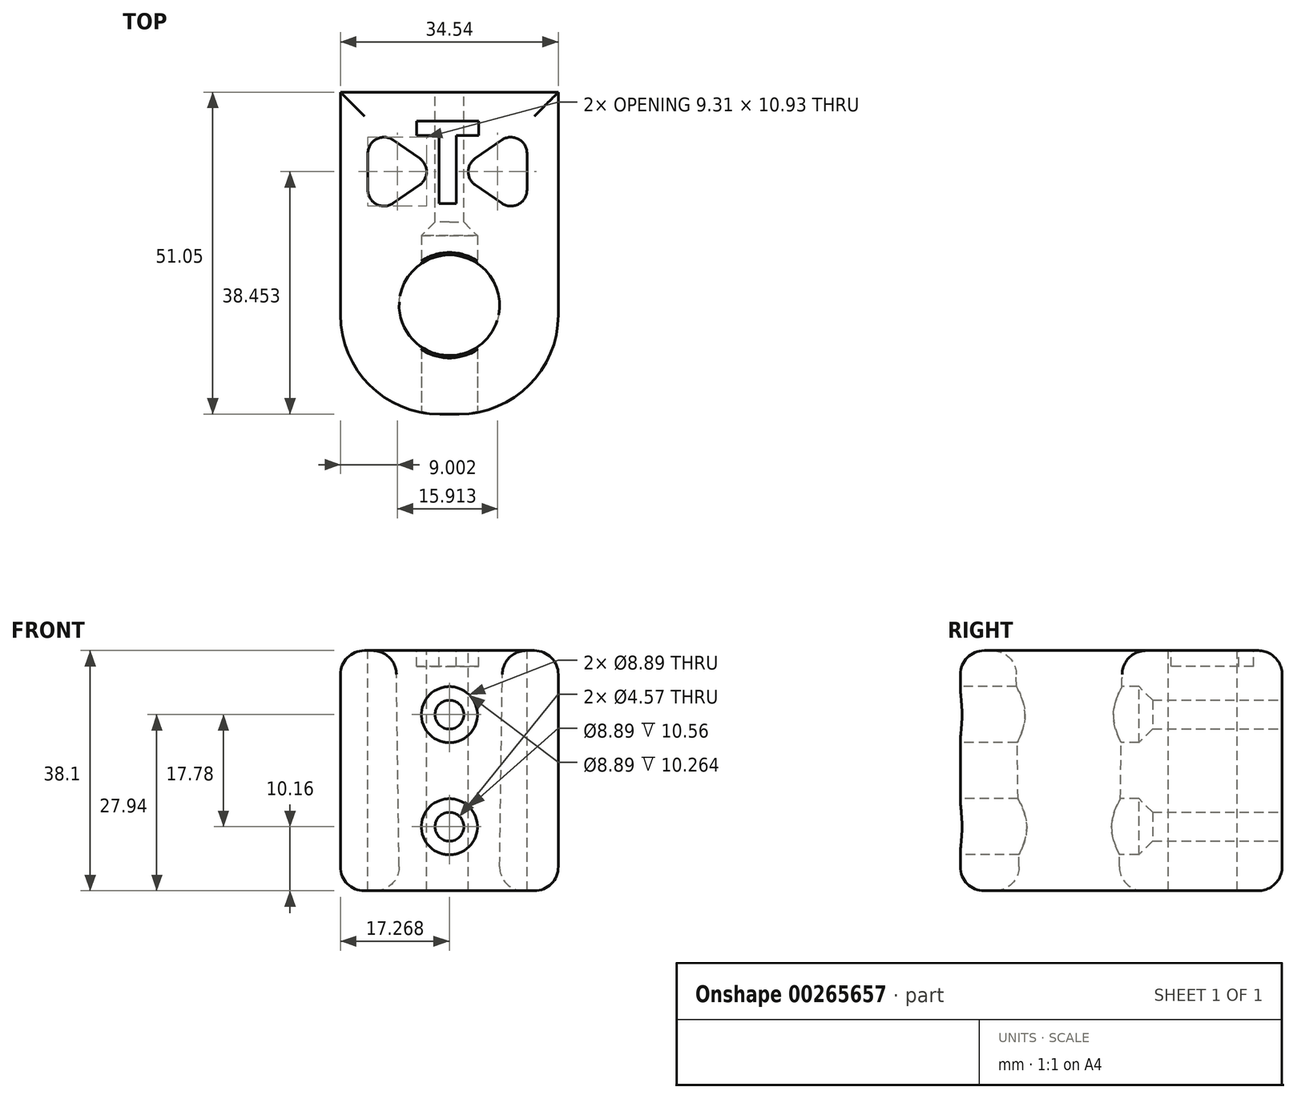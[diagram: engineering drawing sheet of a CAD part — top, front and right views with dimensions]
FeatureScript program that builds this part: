
annotation { "Feature Type Name" : "Feature", "Feature Type Description" : "" }
export const myFeature = defineFeature(function(context is Context, id is Id, definition is map)
    precondition{}
    {
        {
            var Q0;
            Q0=qCreatedBy(makeId("Top.planeOp"),FACE);
            var sketch = newSketch(context, id + "F0", { "sketchPlane" : qUnion([Q0])});
            skLineSegment(sketch, "E0.bottom", {"start": v(0, 0) * mm, "end": v(34.54, 0) * mm});
            skLineSegment(sketch, "E0.top", {"start": v(0, -34.54) * mm, "end": v(34.54, -34.54) * mm});
            skLineSegment(sketch, "E0.left", {"start": v(0, 0) * mm, "end": v(0, -34.54) * mm});
            skLineSegment(sketch, "E0.right", {"start": v(34.54, 0) * mm, "end": v(34.54, -34.54) * mm});
            skSolve(sketch);
        }
        {
            var Q0;
            Q0 = qSketchRegion(id + "F0", true);
            extrude(context, id + "F1", {"entities" : qUnion([Q0]), "depth" : 38.1 * mm});
        }
        {
            var Q0;
            Q0=makeQuery(id+"F1.opExtrude","CAP_FACE",FACE,{"disambiguationData":[OSD([sQuery(id+"F0.wireOp",EDGE,"E0.bottom"),sQuery(id+"F0.wireOp",EDGE,"E0.top"),sQuery(id+"F0.wireOp",EDGE,"E0.left"),sQuery(id+"F0.wireOp",EDGE,"E0.right")])],"isStart":false});
            var sketch = newSketch(context, id + "F2", { "sketchPlane" : qUnion([Q0])});
            skCircle(sketch, "E1", {"center": v(17.27, -17.27) * mm, "radius": 8.45 * mm});
            skPoint(sketch, "E1.centerSnap0", {"position": v(17.27, -34.54) * mm});
            skPoint(sketch, "E1.centerSnap1", {"position": v(34.54, -17.27) * mm});
            skSolve(sketch);
        }
        {
            var Q0;
            Q0=makeQuery(id+"F1.opExtrude","SWEPT_EDGE",EDGE,{"disambiguationData":[OSD([sQuery(id+"F0.wireOp",EDGE,"E0.top"),sQuery(id+"F0.wireOp",EDGE,"E0.right")])]});
            var Q1;
            Q1=makeQuery(id+"F1.opExtrude","SWEPT_EDGE",EDGE,{"disambiguationData":[OSD([sQuery(id+"F0.wireOp",EDGE,"E0.bottom"),sQuery(id+"F0.wireOp",EDGE,"E0.right")])]});
            fillet(context, id + "F3", {"entities" : qUnion([Q0, Q1]), "radius" : 15.75 * mm, "tangentPropagation" : true, "allowEdgeOverflow" : false});
        }
        {
            var Q0;
            Q0=makeQuery(id+"F1.opExtrude","SWEPT_FACE",FACE,{"disambiguationData":[OSD([sQuery(id+"F0.wireOp",EDGE,"E0.left")])]});
            var sketch = newSketch(context, id + "F4", { "sketchPlane" : qUnion([Q0])});
            skCircle(sketch, "E2", {"center": v(17.27, 10.16) * mm, "radius": 2.29 * mm});
            skPoint(sketch, "E2.centerSnap0", {"position": v(17.27, 0) * mm});
            skCircle(sketch, "E3", {"center": v(17.27, 27.94) * mm, "radius": 2.29 * mm});
            skPoint(sketch, "E3.centerSnap0", {"position": v(17.27, 38.1) * mm});
            skSolve(sketch);
        }
        {
            var Q0;
            Q0 = qSketchRegion(id + "F4", true);
            extrude(context, id + "F5", {"entities" : qUnion([Q0]), "operationType" : NewBodyOperationType.REMOVE, "endBound" : BoundingType.THROUGH_ALL, "oppositeDirection" : true, "depth" : 25.4 * mm});
        }
        {
            var Q0;
            {var subQ0=sQuery(id+"F0.wireOp",EDGE,"E0.right");Q0=makeQuery(id+"F5.boolean.opBoolean","SPLIT",FACE,{"disambiguationData":[TD([makeQuery(id+"F3.opFillet","BLEND_FACE",FACE,{"disambiguationData":[OSD([sQuery(id+"F0.wireOp",EDGE,"E0.bottom"),subQ0])]}),makeQuery(id+"F3.opFillet","BLEND_FACE",FACE,{"disambiguationData":[OSD([sQuery(id+"F0.wireOp",EDGE,"E0.top"),subQ0])]}),makeQuery(id+"F5.opExtrude","SWEPT_FACE",FACE,{"disambiguationData":[OSD([sQuery(id+"F4.wireOp",EDGE,"E2")])]}),makeQuery(id+"F5.opExtrude","SWEPT_FACE",FACE,{"disambiguationData":[OSD([sQuery(id+"F4.wireOp",EDGE,"E3")])]})])],"derivedFrom":makeQuery(id+"F1.opExtrude","SWEPT_FACE",FACE,{"disambiguationData":[OSD([subQ0])]})});}
            var sketch = newSketch(context, id + "F6", { "sketchPlane" : qUnion([Q0])});
            skCircle(sketch, "E4", {"center": v(-17.27, 27.94) * mm, "radius": 4.45 * mm});
            skCircle(sketch, "E5", {"center": v(-17.27, 10.16) * mm, "radius": 4.45 * mm});
            skSolve(sketch);
        }
        {
            var Q0;
            Q0 = qSketchRegion(id + "F6", true);
            extrude(context, id + "F7", {"entities" : qUnion([Q0]), "operationType" : NewBodyOperationType.REMOVE, "oppositeDirection" : true, "depth" : 27.94 * mm});
        }
        {
            var Q0;
            Q0=makeQuery(id+"F7.boolean.opBoolean","INTERSECT",EDGE,{"derivedFrom":[makeQuery(id+"F5.boolean.opBoolean","COPY",FACE,{"disambiguationData":[TD([makeQuery(id+"F1.opExtrude","SWEPT_FACE",FACE,{"disambiguationData":[OSD([sQuery(id+"F0.wireOp",EDGE,"E0.left")])]})])],"derivedFrom":makeQuery(id+"F5.opExtrude","SWEPT_FACE",FACE,{"disambiguationData":[OSD([sQuery(id+"F4.wireOp",EDGE,"E3")])]})}),makeQuery(id+"F7.opExtrude","CAP_FACE",FACE,{"disambiguationData":[OSD([sQuery(id+"F6.wireOp",EDGE,"E4")])],"isStart":false})]});
            var Q1;
            Q1=makeQuery(id+"F7.boolean.opBoolean","INTERSECT",EDGE,{"derivedFrom":[makeQuery(id+"F5.boolean.opBoolean","COPY",FACE,{"disambiguationData":[TD([makeQuery(id+"F1.opExtrude","SWEPT_FACE",FACE,{"disambiguationData":[OSD([sQuery(id+"F0.wireOp",EDGE,"E0.left")])]})])],"derivedFrom":makeQuery(id+"F5.opExtrude","SWEPT_FACE",FACE,{"disambiguationData":[OSD([sQuery(id+"F4.wireOp",EDGE,"E2")])]})}),makeQuery(id+"F7.opExtrude","CAP_FACE",FACE,{"disambiguationData":[OSD([sQuery(id+"F6.wireOp",EDGE,"E5")])],"isStart":false})]});
            chamfer(context, id + "F8", {"entities" : qUnion([Q0, Q1]), "width" : 2.54 * mm, "tangentPropagation" : true});
        }
        {
            var Q0;
            Q0=makeQuery(id+"F1.opExtrude","SWEPT_FACE",FACE,{"disambiguationData":[OSD([sQuery(id+"F0.wireOp",EDGE,"E0.left")])]});
            extrude(context, id + "F9", {"entities" : qUnion([Q0]), "operationType" : NewBodyOperationType.ADD, "depth" : 16.5 * mm});
        }
        {
            var Q0;
            Q0 = qSketchRegion(id + "F2", true);
            extrude(context, id + "F10", {"entities" : qUnion([Q0]), "operationType" : NewBodyOperationType.REMOVE, "endBound" : BoundingType.THROUGH_ALL, "oppositeDirection" : true, "depth" : 25.4 * mm, "hasDraft" : true, "draftAngle" : .8 * degree, "draftPullDirection" : true});
        }
        {
            var Q0;
            Q0=makeQuery(id+"F1.opExtrude","CAP_FACE",FACE,{"disambiguationData":[OSD([sQuery(id+"F0.wireOp",EDGE,"E0.bottom"),sQuery(id+"F0.wireOp",EDGE,"E0.top"),sQuery(id+"F0.wireOp",EDGE,"E0.left"),sQuery(id+"F0.wireOp",EDGE,"E0.right")])],"isStart":false});
            fillet(context, id + "F11", {"entities" : qUnion([Q0]), "radius" : 3.8 * mm, "tangentPropagation" : true, "allowEdgeOverflow" : false});
        }
        {
            var Q0;
            Q0=makeQuery(id+"F1.opExtrude","CAP_FACE",FACE,{"disambiguationData":[OSD([sQuery(id+"F0.wireOp",EDGE,"E0.bottom"),sQuery(id+"F0.wireOp",EDGE,"E0.top"),sQuery(id+"F0.wireOp",EDGE,"E0.left"),sQuery(id+"F0.wireOp",EDGE,"E0.right")])],"isStart":true});
            fillet(context, id + "F12", {"entities" : qUnion([Q0]), "radius" : 3.8 * mm, "tangentPropagation" : true, "allowEdgeOverflow" : false});
        }
        {
            var Q0;
            Q0=makeQuery(id+"F1.opExtrude","SWEPT_BODY",BODY,{"disambiguationData":[OSD([sQuery(id+"F0.wireOp",EDGE,"E0.bottom"),sQuery(id+"F0.wireOp",EDGE,"E0.top"),sQuery(id+"F0.wireOp",EDGE,"E0.left"),sQuery(id+"F0.wireOp",EDGE,"E0.right")])]});
            var Q1;
            Q1=makeQuery(id+"F9.opExtrude","CAP_EDGE",EDGE,{"disambiguationData":[OSD([sQuery(id+"F0.wireOp",EDGE,"E0.bottom"),sQuery(id+"F0.wireOp",EDGE,"E0.left")])],"isStart":false});
            transform(context, id + "F13", {"entities" : qUnion([Q0]), "transformType" : TransformType.ROTATION, "transformAxis" : qUnion([Q1]), "angle" : 90 * degree, "makeCopy" : false});
        }
        {
            var Q0;
            {var subQ0=sQuery(id+"F0.wireOp",EDGE,"E0.left");Q0=makeQuery(id+"F9.boolean.opBoolean","MERGE",FACE,{"derivedFrom":[makeQuery(id+"F1.opExtrude","CAP_FACE",FACE,{"disambiguationData":[OSD([sQuery(id+"F0.wireOp",EDGE,"E0.bottom"),sQuery(id+"F0.wireOp",EDGE,"E0.top"),subQ0,sQuery(id+"F0.wireOp",EDGE,"E0.right")])],"isStart":false}),makeQuery(id+"F9.opExtrude","SWEPT_FACE",FACE,{"disambiguationData":[OSD([subQ0]),TDD([makeQuery(id+"F1.opExtrude","CAP_EDGE",EDGE,{"disambiguationData":[OSD([subQ0])],"isStart":false})])]})]});}
            var sketch = newSketch(context, id + "F14", { "sketchPlane" : qUnion([Q0])});
            skLineSegment(sketch, "E6", {"start": v(-25.47, -7.58) * mm, "end": v(-29.7, -10.5) * mm});
            skLineSegment(sketch, "E7", {"start": v(-21.48, -9.67) * mm, "end": v(-21.48, -15.52) * mm});
            skLineSegment(sketch, "E8", {"start": v(-25.47, -17.61) * mm, "end": v(-29.7, -14.69) * mm});
            skArc(sketch, "E9.filletArc", {"start": v(-21.48, -9.67) * mm, "mid": v(-22.84, -7.42) * mm, "end": v(-25.47, -7.58) * mm});
            skArc(sketch, "E10.filletArc", {"start": v(-25.47, -17.61) * mm, "mid": v(-22.84, -17.77) * mm, "end": v(-21.48, -15.52) * mm});
            skArc(sketch, "E11.filletArc", {"start": v(-29.7, -10.5) * mm, "mid": v(-30.8, -12.6) * mm, "end": v(-29.7, -14.69) * mm});
            skLineSegment(sketch, "E12", {"start": v(-42.72, -17.61) * mm, "end": v(-38.49, -14.69) * mm});
            skLineSegment(sketch, "E13", {"start": v(-46.7, -15.52) * mm, "end": v(-46.7, -9.67) * mm});
            skLineSegment(sketch, "E14", {"start": v(-42.72, -7.58) * mm, "end": v(-38.49, -10.5) * mm});
            skArc(sketch, "E15.filletArc", {"start": v(-46.7, -15.52) * mm, "mid": v(-45.34, -17.77) * mm, "end": v(-42.72, -17.61) * mm});
            skArc(sketch, "E16.filletArc", {"start": v(-42.72, -7.58) * mm, "mid": v(-45.34, -7.42) * mm, "end": v(-46.7, -9.67) * mm});
            skArc(sketch, "E17.filletArc", {"start": v(-38.49, -14.69) * mm, "mid": v(-37.4, -12.6) * mm, "end": v(-38.49, -10.5) * mm});
            skLineSegment(sketch, "E18", {"start": v(-33.78, 0) * mm, "end": v(-33.78, -25.39) * mm, "construction": true});
            skLineSegment(sketch, "E19", {"start": v(-33.78, -12.7) * mm, "end": v(-20.32, -12.6) * mm, "construction": true});
            skLineSegment(sketch, "E20", {"start": v(-33.78, -25.39) * mm, "end": v(-16.51, -25.39) * mm, "construction": true});
            skLineSegment(sketch, "E21", {"start": v(-16.51, -25.39) * mm, "end": v(-51.05, -25.28) * mm, "construction": true});
            skPoint(sketch, "E22", {"position": v(-46.7, -12.6) * mm});
            skPoint(sketch, "E23", {"position": v(-21.48, -14.7) * mm});
            skSolve(sketch);
        }
        {
            var Q0;
            Q0 = qSketchRegion(id + "F14", true);
            extrude(context, id + "F15", {"entities" : qUnion([Q0]), "operationType" : NewBodyOperationType.REMOVE, "endBound" : BoundingType.THROUGH_ALL, "oppositeDirection" : true, "depth" : 25.4 * mm});
        }
        {
            var Q0;
            {var subQ0=sQuery(id+"F0.wireOp",EDGE,"E0.left");Q0=makeQuery(id+"F9.boolean.opBoolean","MERGE",FACE,{"derivedFrom":[makeQuery(id+"F1.opExtrude","CAP_FACE",FACE,{"disambiguationData":[OSD([sQuery(id+"F0.wireOp",EDGE,"E0.bottom"),sQuery(id+"F0.wireOp",EDGE,"E0.top"),subQ0,sQuery(id+"F0.wireOp",EDGE,"E0.right")])],"isStart":false}),makeQuery(id+"F9.opExtrude","SWEPT_FACE",FACE,{"disambiguationData":[OSD([subQ0]),TDD([makeQuery(id+"F1.opExtrude","CAP_EDGE",EDGE,{"disambiguationData":[OSD([subQ0])],"isStart":false})])]})]});}
            var sketch = newSketch(context, id + "F16", { "sketchPlane" : qUnion([Q0])});
            skText(sketch, "E24", { "text": "T", "fontName": "OpenSans-Bold.ttf"});
            skLineSegment(sketch, "E25", {"start": v(-33.66, -3.8) * mm, "end": v(-33.66, -20.1) * mm, "construction": true});
            const initialGuessF16  = {"E24": [-0.03937, -0.01764, 1, 0, 0.0132]};
            skSetInitialGuess(sketch, initialGuessF16);
            skSolve(sketch);
        }
        {
            var Q0;
            Q0 = qSketchRegion(id + "F16", true);
            extrude(context, id + "F17", {"entities" : qUnion([Q0]), "operationType" : NewBodyOperationType.REMOVE, "oppositeDirection" : true, "depth" : 2.54 * mm});
        }
    });
